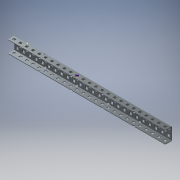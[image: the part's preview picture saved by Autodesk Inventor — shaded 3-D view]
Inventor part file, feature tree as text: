
AUTODESK INVENTOR PART (.ipt)
format: ipt  version: 2018 (Build 220112000, 112)  size: 2,676,736 bytes
history: native  units: mm (DEFAULTED — no unit token found)
features: other x124, extrude x124, sketch x3, pattern_linear x3, imported_body x1, plane x1, mirror x1
ambient origin geometry x8: Origin, YZ Plane, XZ Plane, XY Plane, X Axis, Y Axis, Z Axis, Center Point
bodies: Solid1 (feature_tree)
feature tree (257):
  imported_body  "Base1"
  sketch  "Sketch1"  dims[d1=1.1684mm]
  pattern_linear  "Rectangular Pattern1"  Spacing1=0.0mm  [1 undecoded]
  pattern_linear  "Rectangular Pattern2"  Count1=25  [1 undecoded]
  pattern_linear  "Rectangular Pattern3"  Spacing1=12.7mm  [1 undecoded]
  plane  "Work Plane1"
  mirror  "Mirror1"
  sketch  "Sketch3"  dims[d3=1.1684mm d4=0.0mm d5=250.0mm d7=12.7mm d8=20.0mm d10=12.7mm d11=240.0mm d13=12.7mm d14=1.1684mm d15=0.0mm d16=250.0mm d18=12.7mm d19=0.0mm d20=0.0mm d21=0.0mm d22=0.0mm d23=0.0mm d24=0.0mm d25=0.0mm d26=0.0mm d27=0.0mm d28=0.0mm d29=0.0mm d30=0.0mm d31=0.0mm d32=0.0mm d33=0.0mm d34=0.0mm d35=0.0mm d36=0.0mm d37=0.0mm d38=0.0mm d39=0.0mm d40=0.0mm d41=0.0mm d42=0.0mm d43=0.0mm d44=0.0mm d45=0.0mm d46=0.0mm d47=0.0mm d48=0.0mm d49=0.0mm d50=0.0mm d51=0.0mm d52=0.0mm d53=0.0mm d54=0.0mm d55=0.0mm d56=0.0mm d57=0.0mm d58=0.0mm d59=0.0mm d60=0.0mm d61=0.0mm d62=0.0mm d63=0.0mm d64=0.0mm d65=0.0mm d66=0.0mm d67=0.0mm d68=0.0mm d69=0.0mm d70=0.0mm d71=0.0mm d72=0.0mm d73=0.0mm d74=0.0mm d75=0.0mm d76=0.0mm d77=0.0mm d78=0.0mm d79=0.0mm d80=0.0mm d81=0.0mm d82=0.0mm d83=0.0mm d84=0.0mm d85=0.0mm d86=0.0mm d87=0.0mm d88=0.0mm d89=0.0mm d90=0.0mm d91=0.0mm d92=0.0mm d93=0.0mm d94=0.0mm d95=0.0mm d96=0.0mm d97=0.0mm d98=0.0mm d99=0.0mm d100=0.0mm d101=0.0mm d102=0.0mm d103=0.0mm d104=0.0mm d105=0.0mm d106=0.0mm d107=0.0mm d108=0.0mm d109=0.0mm d110=0.0mm d111=0.0mm d112=0.0mm d113=0.0mm d114=0.0mm d115=0.0mm d116=0.0mm d117=0.0mm d118=0.0mm d119=0.0mm d120=0.0mm d121=0.0mm d122=0.0mm d123=0.0mm d124=0.0mm d125=0.0mm d126=0.0mm d127=0.0mm d128=0.0mm d129=0.0mm d130=0.0mm d131=0.0mm d132=0.0mm d133=0.0mm d134=0.0mm d135=0.0mm d136=0.0mm d137=0.0mm d138=0.0mm d139=0.0mm d140=0.0mm d141=0.0mm d142=0.0mm d143=0.0mm d144=0.0mm d145=0.0mm d146=0.0mm d147=0.0mm d148=0.0mm d149=0.0mm d150=0.0mm d151=0.0mm d152=0.0mm d153=0.0mm d154=0.0mm d155=0.0mm d156=0.0mm d157=0.0mm d158=0.0mm d159=0.0mm d160=0.0mm d161=0.0mm d162=0.0mm d163=0.0mm d164=0.0mm d165=0.0mm d166=0.0mm d167=0.0mm d168=0.0mm d169=0.0mm d170=0.0mm d171=0.0mm d172=0.0mm d173=0.0mm d174=0.0mm d175=0.0mm d176=0.0mm d177=0.0mm d178=0.0mm d179=0.0mm d180=0.0mm d181=0.0mm d182=0.0mm d183=0.0mm d184=0.0mm d185=0.0mm d186=0.0mm d187=0.0mm d188=0.0mm d189=0.0mm d190=0.0mm d191=0.0mm d192=0.0mm d193=0.0mm d194=0.0mm d195=0.0mm d196=0.0mm d197=0.0mm d198=0.0mm d199=0.0mm d200=0.0mm d201=0.0mm d202=0.0mm d203=0.0mm d204=0.0mm d205=0.0mm d206=0.0mm d207=0.0mm d208=0.0mm d209=0.0mm d210=0.0mm d211=0.0mm d212=0.0mm d213=0.0mm d214=0.0mm d215=0.0mm d216=0.0mm d217=0.0mm d218=0.0mm d219=0.0mm d220=0.0mm d221=0.0mm d222=0.0mm d223=0.0mm d224=0.0mm d225=0.0mm d226=0.0mm d227=0.0mm d228=0.0mm d229=0.0mm d230=0.0mm d231=0.0mm d232=0.0mm d233=0.0mm d234=0.0mm d235=0.0mm d236=0.0mm d237=0.0mm d238=0.0mm d239=0.0mm d240=0.0mm d241=0.0mm d242=0.0mm d243=0.0mm d244=0.0mm d245=0.0mm d246=0.0mm d247=0.0mm d248=0.0mm d249=0.0mm d250=0.0mm d251=0.0mm d252=0.0mm d253=0.0mm d254=0.0mm d255=0.0mm d256=0.0mm d257=0.0mm d258=0.0mm d259=0.0mm d260=0.0mm d261=0.0mm d262=0.0mm d263=0.0mm]
  other  "Srf1"
  other  "Srf2"
  other  "Srf3"
  other  "Srf4"
  other  "Srf5"
  other  "Srf6"
  other  "Srf7"
  other  "Srf8"
  other  "Srf9"
  other  "Srf10"
  other  "Srf11"
  other  "Srf12"
  other  "Srf13"
  other  "Srf14"
  other  "Srf15"
  other  "Srf16"
  other  "Srf17"
  other  "Srf18"
  other  "Srf19"
  other  "Srf20"
  other  "Srf21"
  other  "Srf22"
  other  "Srf23"
  other  "Srf24"
  other  "Srf25"
  other  "Srf26"
  other  "Srf27"
  other  "Srf28"
  other  "Srf29"
  other  "Srf30"
  other  "Srf31"
  other  "Srf32"
  other  "Srf33"
  other  "Srf34"
  other  "Srf35"
  other  "Srf36"
  other  "Srf37"
  other  "Srf38"
  other  "Srf39"
  other  "Srf40"
  other  "Srf41"
  other  "Srf42"
  other  "Srf43"
  other  "Srf44"
  other  "Srf45"
  other  "Srf46"
  other  "Srf47"
  other  "Srf48"
  other  "Srf49"
  other  "Srf50"
  other  "Srf51"
  other  "Srf52"
  other  "Srf53"
  other  "Srf54"
  other  "Srf55"
  other  "Srf56"
  other  "Srf57"
  other  "Srf58"
  other  "Srf59"
  other  "Srf60"
  other  "Srf61"
  other  "Srf62"
  other  "Srf63"
  other  "Srf64"
  other  "Srf65"
  other  "Srf66"
  other  "Srf67"
  other  "Srf68"
  other  "Srf69"
  other  "Srf70"
  other  "Srf71"
  other  "Srf72"
  other  "Srf73"
  other  "Srf74"
  sketch  "Sketch2"  dims[d2=0.0mm]
  other  "Srf75"
  other  "Srf76"
  other  "Srf77"
  other  "Srf78"
  other  "Srf79"
  other  "Srf80"
  other  "Srf81"
  other  "Srf82"
  other  "Srf83"
  other  "Srf84"
  other  "Srf85"
  other  "Srf86"
  other  "Srf87"
  other  "Srf88"
  other  "Srf89"
  other  "Srf90"
  other  "Srf91"
  other  "Srf92"
  other  "Srf93"
  other  "Srf94"
  other  "Srf95"
  other  "Srf96"
  other  "Srf97"
  other  "Srf98"
  other  "Srf99"
  other  "Srf100"
  other  "Srf101"
  other  "Srf102"
  other  "Srf103"
  other  "Srf104"
  other  "Srf105"
  other  "Srf106"
  other  "Srf107"
  other  "Srf108"
  other  "Srf109"
  other  "Srf110"
  other  "Srf111"
  other  "Srf112"
  other  "Srf113"
  other  "Srf114"
  other  "Srf115"
  other  "Srf116"
  other  "Srf117"
  other  "Srf118"
  other  "Srf119"
  other  "Srf120"
  other  "Srf121"
  other  "Srf122"
  other  "Srf123"
  other  "Srf124"
  extrude  "ExtrusionSrf1"  Depth=20.0mm
  extrude  "ExtrusionSrf2"  Depth=240.0mm
  extrude  "ExtrusionSrf75"  Depth=12.7mm
  extrude  "ExtrusionSrf3"  Depth=1.1684mm
  extrude  "ExtrusionSrf4"  TaperAngle=0.0deg  [1 undecoded]
  extrude  "ExtrusionSrf5"  Depth=250.0mm
  extrude  "ExtrusionSrf6"  Depth=12.7mm
  extrude  "ExtrusionSrf7"  TaperAngle=0.0deg  [1 undecoded]
  extrude  "ExtrusionSrf8"  TaperAngle=0.0deg  [1 undecoded]
  extrude  "ExtrusionSrf9"  TaperAngle=0.0deg  [1 undecoded]
  extrude  "ExtrusionSrf10"  TaperAngle=0.0deg  [1 undecoded]
  extrude  "ExtrusionSrf11"  TaperAngle=0.0deg  [1 undecoded]
  extrude  "ExtrusionSrf12"  TaperAngle=0.0deg  [1 undecoded]
  extrude  "ExtrusionSrf13"  TaperAngle=0.0deg  [1 undecoded]
  extrude  "ExtrusionSrf14"  TaperAngle=0.0deg  [1 undecoded]
  extrude  "ExtrusionSrf15"  TaperAngle=0.0deg  [1 undecoded]
  extrude  "ExtrusionSrf16"  TaperAngle=0.0deg  [1 undecoded]
  extrude  "ExtrusionSrf17"  TaperAngle=0.0deg  [1 undecoded]
  extrude  "ExtrusionSrf18"  TaperAngle=0.0deg  [1 undecoded]
  extrude  "ExtrusionSrf19"  TaperAngle=0.0deg  [1 undecoded]
  extrude  "ExtrusionSrf20"  TaperAngle=0.0deg  [1 undecoded]
  extrude  "ExtrusionSrf21"  TaperAngle=0.0deg  [1 undecoded]
  extrude  "ExtrusionSrf22"  TaperAngle=0.0deg  [1 undecoded]
  extrude  "ExtrusionSrf23"  TaperAngle=0.0deg  [1 undecoded]
  extrude  "ExtrusionSrf24"  TaperAngle=0.0deg  [1 undecoded]
  extrude  "ExtrusionSrf25"  TaperAngle=0.0deg  [1 undecoded]
  extrude  "ExtrusionSrf26"  TaperAngle=0.0deg  [1 undecoded]
  extrude  "ExtrusionSrf27"  TaperAngle=0.0deg  [1 undecoded]
  extrude  "ExtrusionSrf28"  TaperAngle=0.0deg  [1 undecoded]
  extrude  "ExtrusionSrf29"  TaperAngle=0.0deg  [1 undecoded]
  extrude  "ExtrusionSrf30"  TaperAngle=0.0deg  [1 undecoded]
  extrude  "ExtrusionSrf31"  TaperAngle=0.0deg  [1 undecoded]
  extrude  "ExtrusionSrf32"  TaperAngle=0.0deg  [1 undecoded]
  extrude  "ExtrusionSrf33"  TaperAngle=0.0deg  [1 undecoded]
  extrude  "ExtrusionSrf34"  TaperAngle=0.0deg  [1 undecoded]
  extrude  "ExtrusionSrf35"  TaperAngle=0.0deg  [1 undecoded]
  extrude  "ExtrusionSrf36"  TaperAngle=0.0deg  [1 undecoded]
  extrude  "ExtrusionSrf37"  TaperAngle=0.0deg  [1 undecoded]
  extrude  "ExtrusionSrf38"  TaperAngle=0.0deg  [1 undecoded]
  extrude  "ExtrusionSrf39"  TaperAngle=0.0deg  [1 undecoded]
  extrude  "ExtrusionSrf40"  TaperAngle=0.0deg  [1 undecoded]
  extrude  "ExtrusionSrf41"  TaperAngle=0.0deg  [1 undecoded]
  extrude  "ExtrusionSrf42"  TaperAngle=0.0deg  [1 undecoded]
  extrude  "ExtrusionSrf43"  TaperAngle=0.0deg  [1 undecoded]
  extrude  "ExtrusionSrf44"  TaperAngle=0.0deg  [1 undecoded]
  extrude  "ExtrusionSrf45"  TaperAngle=0.0deg  [1 undecoded]
  extrude  "ExtrusionSrf46"  TaperAngle=0.0deg  [1 undecoded]
  extrude  "ExtrusionSrf47"  TaperAngle=0.0deg  [1 undecoded]
  extrude  "ExtrusionSrf48"  TaperAngle=0.0deg  [1 undecoded]
  extrude  "ExtrusionSrf49"  TaperAngle=0.0deg  [1 undecoded]
  extrude  "ExtrusionSrf50"  TaperAngle=0.0deg  [1 undecoded]
  extrude  "ExtrusionSrf51"  TaperAngle=0.0deg  [1 undecoded]
  extrude  "ExtrusionSrf52"  TaperAngle=0.0deg  [1 undecoded]
  extrude  "ExtrusionSrf53"  TaperAngle=0.0deg  [1 undecoded]
  extrude  "ExtrusionSrf54"  TaperAngle=0.0deg  [1 undecoded]
  extrude  "ExtrusionSrf55"  TaperAngle=0.0deg  [1 undecoded]
  extrude  "ExtrusionSrf56"  TaperAngle=0.0deg  [1 undecoded]
  extrude  "ExtrusionSrf57"  TaperAngle=0.0deg  [1 undecoded]
  extrude  "ExtrusionSrf58"  TaperAngle=0.0deg  [1 undecoded]
  extrude  "ExtrusionSrf59"  TaperAngle=0.0deg  [1 undecoded]
  extrude  "ExtrusionSrf60"  TaperAngle=0.0deg  [1 undecoded]
  extrude  "ExtrusionSrf61"  TaperAngle=0.0deg  [1 undecoded]
  extrude  "ExtrusionSrf62"  TaperAngle=0.0deg  [1 undecoded]
  extrude  "ExtrusionSrf63"  TaperAngle=0.0deg  [1 undecoded]
  extrude  "ExtrusionSrf64"  TaperAngle=0.0deg  [1 undecoded]
  extrude  "ExtrusionSrf65"  TaperAngle=0.0deg  [1 undecoded]
  extrude  "ExtrusionSrf66"  TaperAngle=0.0deg  [1 undecoded]
  extrude  "ExtrusionSrf67"  TaperAngle=0.0deg  [1 undecoded]
  extrude  "ExtrusionSrf68"  TaperAngle=0.0deg  [1 undecoded]
  extrude  "ExtrusionSrf69"  TaperAngle=0.0deg  [1 undecoded]
  extrude  "ExtrusionSrf70"  TaperAngle=0.0deg  [1 undecoded]
  extrude  "ExtrusionSrf71"  TaperAngle=0.0deg  [1 undecoded]
  extrude  "ExtrusionSrf72"  TaperAngle=0.0deg  [1 undecoded]
  extrude  "ExtrusionSrf73"  TaperAngle=0.0deg  [1 undecoded]
  extrude  "ExtrusionSrf74"  TaperAngle=0.0deg  [1 undecoded]
  extrude  "ExtrusionSrf76"  TaperAngle=0.0deg  [1 undecoded]
  extrude  "ExtrusionSrf77"  TaperAngle=0.0deg  [1 undecoded]
  extrude  "ExtrusionSrf78"  TaperAngle=0.0deg  [1 undecoded]
  extrude  "ExtrusionSrf79"  TaperAngle=0.0deg  [1 undecoded]
  extrude  "ExtrusionSrf80"  TaperAngle=0.0deg  [1 undecoded]
  extrude  "ExtrusionSrf81"  TaperAngle=0.0deg  [1 undecoded]
  extrude  "ExtrusionSrf82"  TaperAngle=0.0deg  [1 undecoded]
  extrude  "ExtrusionSrf83"  TaperAngle=0.0deg  [1 undecoded]
  extrude  "ExtrusionSrf84"  TaperAngle=0.0deg  [1 undecoded]
  extrude  "ExtrusionSrf85"  TaperAngle=0.0deg  [1 undecoded]
  extrude  "ExtrusionSrf86"  TaperAngle=0.0deg  [1 undecoded]
  extrude  "ExtrusionSrf87"  TaperAngle=0.0deg  [1 undecoded]
  extrude  "ExtrusionSrf88"  TaperAngle=0.0deg  [1 undecoded]
  extrude  "ExtrusionSrf89"  TaperAngle=0.0deg  [1 undecoded]
  extrude  "ExtrusionSrf90"  TaperAngle=0.0deg  [1 undecoded]
  extrude  "ExtrusionSrf91"  TaperAngle=0.0deg  [1 undecoded]
  extrude  "ExtrusionSrf92"  TaperAngle=0.0deg  [1 undecoded]
  extrude  "ExtrusionSrf93"  TaperAngle=0.0deg  [1 undecoded]
  extrude  "ExtrusionSrf94"  TaperAngle=0.0deg  [1 undecoded]
  extrude  "ExtrusionSrf95"  TaperAngle=0.0deg  [1 undecoded]
  extrude  "ExtrusionSrf96"  TaperAngle=0.0deg  [1 undecoded]
  extrude  "ExtrusionSrf97"  TaperAngle=0.0deg  [1 undecoded]
  extrude  "ExtrusionSrf98"  TaperAngle=0.0deg  [1 undecoded]
  extrude  "ExtrusionSrf99"  TaperAngle=0.0deg  [1 undecoded]
  extrude  "ExtrusionSrf100"  TaperAngle=0.0deg  [1 undecoded]
  extrude  "ExtrusionSrf101"  TaperAngle=0.0deg  [1 undecoded]
  extrude  "ExtrusionSrf102"  TaperAngle=0.0deg  [1 undecoded]
  extrude  "ExtrusionSrf103"  TaperAngle=0.0deg  [1 undecoded]
  extrude  "ExtrusionSrf104"  TaperAngle=0.0deg  [1 undecoded]
  extrude  "ExtrusionSrf105"  TaperAngle=0.0deg  [1 undecoded]
  extrude  "ExtrusionSrf106"  TaperAngle=0.0deg  [1 undecoded]
  extrude  "ExtrusionSrf107"  TaperAngle=0.0deg  [1 undecoded]
  extrude  "ExtrusionSrf108"  TaperAngle=0.0deg  [1 undecoded]
  extrude  "ExtrusionSrf109"  TaperAngle=0.0deg  [1 undecoded]
  extrude  "ExtrusionSrf110"  TaperAngle=0.0deg  [1 undecoded]
  extrude  "ExtrusionSrf111"  TaperAngle=0.0deg  [1 undecoded]
  extrude  "ExtrusionSrf112"  TaperAngle=0.0deg  [1 undecoded]
  extrude  "ExtrusionSrf113"  TaperAngle=0.0deg  [1 undecoded]
  extrude  "ExtrusionSrf114"  TaperAngle=0.0deg  [1 undecoded]
  extrude  "ExtrusionSrf115"  TaperAngle=0.0deg  [1 undecoded]
  extrude  "ExtrusionSrf116"  TaperAngle=0.0deg  [1 undecoded]
  extrude  "ExtrusionSrf117"  TaperAngle=0.0deg  [1 undecoded]
  extrude  "ExtrusionSrf118"  TaperAngle=0.0deg  [1 undecoded]
  extrude  "ExtrusionSrf119"  TaperAngle=0.0deg  [1 undecoded]
  extrude  "ExtrusionSrf120"  TaperAngle=0.0deg  [1 undecoded]
  extrude  "ExtrusionSrf121"  TaperAngle=0.0deg  [1 undecoded]
  extrude  "ExtrusionSrf122"  TaperAngle=0.0deg  [1 undecoded]
  extrude  "ExtrusionSrf123"  TaperAngle=0.0deg  [1 undecoded]
  extrude  "ExtrusionSrf124"  TaperAngle=0.0deg  [1 undecoded]
note: 121 required parameter values undecoded (feature->parameter linkage not recoverable at this tier; creation-order binding heuristic only, values carry confidence <= 0.55)
